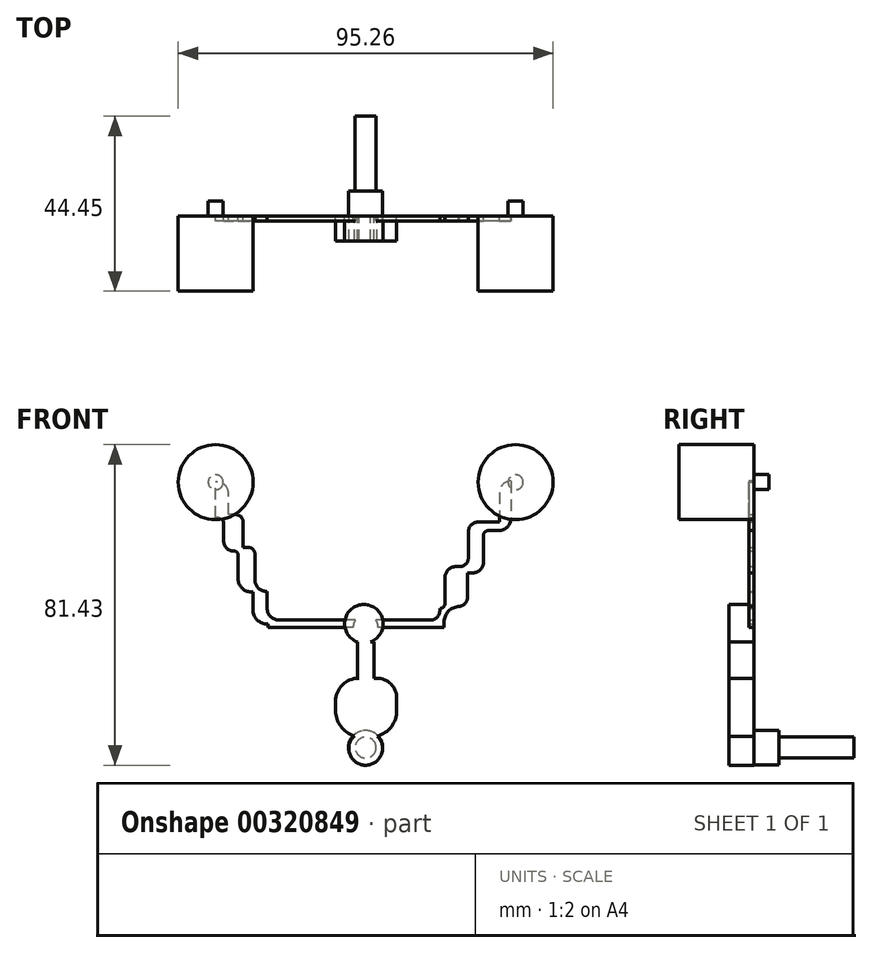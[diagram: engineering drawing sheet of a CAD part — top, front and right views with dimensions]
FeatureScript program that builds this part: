
annotation { "Feature Type Name" : "Feature", "Feature Type Description" : "" }
export const myFeature = defineFeature(function(context is Context, id is Id, definition is map)
    precondition{}
    {
        {
            var Q0;
            Q0=qCreatedBy(makeId("Front.planeOp"),FACE);
            var sketch = newSketch(context, id + "F0", { "sketchPlane" : qUnion([Q0])});
            skCircle(sketch, "E0", {"center": v(-38.1, 36.84) * mm, "radius": 9.53 * mm});
            skCircle(sketch, "E1", {"center": v(38.1, 36.84) * mm, "radius": 9.53 * mm});
            skSolve(sketch);
        }
        {
            var Q0;
            Q0 = qSketchRegion(id + "F0", true);
            var Q1;
            Q1=makeQuery(id+"F0.imprint","IMPRINT",FACE,{"disambiguationData":[TD([[makeQuery(id+"F0.imprint","IMPRINT",EDGE,{"derivedFrom":sQuery(id+"F0.wireOp",EDGE,"W35FGYUQ-ZzTs-Mg4Y-dGm8-Tc2TrGyiYf4W")}),1.0]])]});
            extrude(context, id + "F1", {"entities" : qUnion([Q0, Q1]), "depth" : 19.05 * mm});
        }
        {
            var Q0;
            Q0=qCreatedBy(makeId("Front.planeOp"),FACE);
            var sketch = newSketch(context, id + "F2", { "sketchPlane" : qUnion([Q0])});
            skCircle(sketch, "E2", {"center": v(-38.1, 36.84) * mm, "radius": 1.9 * mm});
            skCircle(sketch, "E3", {"center": v(38.1, 36.84) * mm, "radius": 1.9 * mm});
            skSolve(sketch);
        }
        {
            var Q0;
            Q0 = qSketchRegion(id + "F2", true);
            extrude(context, id + "F3", {"entities" : qUnion([Q0]), "oppositeDirection" : true, "depth" : 3.8 * mm});
        }
        {
            var Q0;
            Q0=qCreatedBy(makeId("Front.planeOp"),FACE);
            var sketch = newSketch(context, id + "F4", { "sketchPlane" : qUnion([Q0])});
            skPoint(sketch, "E4.2.internal.orphan", {"position": v(-38.1, 36.84) * mm});
            skArc(sketch, "E5", {"start": v(3.18, 0) * mm, "mid": v(3.03, 0.94) * mm, "end": v(2.61, 1.8) * mm});
            skLineSegment(sketch, "E6.bottom", {"start": v(36.89, 37.1) * mm, "end": v(36.86, 37.1) * mm});
            skLineSegment(sketch, "E6.top", {"start": v(33.85, 24.55) * mm, "end": v(31.23, 24.55) * mm});
            skLineSegment(sketch, "E6.left", {"start": v(36.86, 37.1) * mm, "end": v(36.86, 27.56) * mm});
            skLineSegment(sketch, "E6.right", {"start": v(34.06, 34.28) * mm, "end": v(34.06, 26.68) * mm});
            skLineSegment(sketch, "E7.bottom", {"start": v(34.06, 26.68) * mm, "end": v(28.54, 26.68) * mm});
            skLineSegment(sketch, "E7.top", {"start": v(27.32, 13.81) * mm, "end": v(25.92, 13.81) * mm});
            skLineSegment(sketch, "E7.left", {"start": v(29.9, 23.2) * mm, "end": v(29.9, 16.39) * mm});
            skLineSegment(sketch, "E7.right", {"start": v(26.1, 24.24) * mm, "end": v(26.1, 17.61) * mm});
            skLineSegment(sketch, "E8.bottom", {"start": v(23.87, 15.39) * mm, "end": v(22.96, 15.39) * mm});
            skLineSegment(sketch, "E8.top", {"start": v(23.82, 5.23) * mm, "end": v(23.53, 5.23) * mm});
            skLineSegment(sketch, "E8.left", {"start": v(25.92, 13.81) * mm, "end": v(25.92, 7.62) * mm});
            skLineSegment(sketch, "E8.right", {"start": v(20.14, 12.56) * mm, "end": v(20.14, 5.93) * mm});
            skLineSegment(sketch, "E9.bottom", {"start": v(19, 4.8) * mm, "end": v(18.83, 4.8) * mm});
            skLineSegment(sketch, "E9.top", {"start": v(19.95, 0) * mm, "end": v(18.83, 0) * mm});
            skLineSegment(sketch, "E9.left", {"start": v(19.95, 1.37) * mm, "end": v(19.95, 0) * mm});
            skLineSegment(sketch, "E9.right", {"start": v(18.83, 4.8) * mm, "end": v(18.83, 4.14) * mm});
            skLineSegment(sketch, "E10.bottom", {"start": v(18.83, 0) * mm, "end": v(2.61, 0) * mm});
            skLineSegment(sketch, "E10.top", {"start": v(16.48, 1.8) * mm, "end": v(2.61, 1.8) * mm});
            skPoint(sketch, "E11.visualSharp", {"position": v(34.06, 37.1) * mm});
            skArc(sketch, "E11.filletArc", {"start": v(36.89, 37.1) * mm, "mid": v(34.89, 36.28) * mm, "end": v(34.06, 34.28) * mm});
            skPoint(sketch, "E12.visualSharp", {"position": v(36.86, 24.55) * mm});
            skArc(sketch, "E12.filletArc", {"start": v(33.85, 24.55) * mm, "mid": v(35.98, 25.43) * mm, "end": v(36.86, 27.56) * mm});
            skPoint(sketch, "E13.visualSharp", {"position": v(29.9, 24.55) * mm});
            skArc(sketch, "E13.filletArc", {"start": v(31.23, 24.55) * mm, "mid": v(30.29, 24.15) * mm, "end": v(29.9, 23.2) * mm});
            skPoint(sketch, "E14.visualSharp", {"position": v(29.9, 13.81) * mm});
            skArc(sketch, "E14.filletArc", {"start": v(27.32, 13.81) * mm, "mid": v(29.14, 14.57) * mm, "end": v(29.9, 16.39) * mm});
            skPoint(sketch, "E15.visualSharp", {"position": v(26.1, 15.39) * mm});
            skArc(sketch, "E15.filletArc", {"start": v(23.87, 15.39) * mm, "mid": v(25.44, 16.04) * mm, "end": v(26.1, 17.61) * mm});
            skPoint(sketch, "E16.visualSharp", {"position": v(26.1, 26.68) * mm});
            skArc(sketch, "E16.filletArc", {"start": v(28.54, 26.68) * mm, "mid": v(26.8, 25.97) * mm, "end": v(26.1, 24.24) * mm});
            skPoint(sketch, "E17.visualSharp", {"position": v(20.14, 15.39) * mm});
            skArc(sketch, "E17.filletArc", {"start": v(22.96, 15.39) * mm, "mid": v(20.97, 14.56) * mm, "end": v(20.14, 12.56) * mm});
            skPoint(sketch, "E18.visualSharp", {"position": v(25.92, 5.23) * mm});
            skArc(sketch, "E18.filletArc", {"start": v(23.53, 5.23) * mm, "mid": v(25.22, 5.93) * mm, "end": v(25.92, 7.62) * mm});
            skPoint(sketch, "E19.visualSharp", {"position": v(19.95, 5.23) * mm});
            skArc(sketch, "E19.filletArc", {"start": v(23.82, 5.23) * mm, "mid": v(21.08, 4.1) * mm, "end": v(19.95, 1.37) * mm});
            skPoint(sketch, "E20.visualSharp", {"position": v(20.14, 4.8) * mm});
            skArc(sketch, "E20.filletArc", {"start": v(19, 4.8) * mm, "mid": v(19.8, 5.13) * mm, "end": v(20.14, 5.93) * mm});
            skPoint(sketch, "E21.visualSharp", {"position": v(18.83, 1.8) * mm});
            skArc(sketch, "E21.filletArc", {"start": v(16.48, 1.8) * mm, "mid": v(18.14, 2.49) * mm, "end": v(18.83, 4.14) * mm});
            skLineSegment(sketch, "E22.bottom", {"start": v(-2.61, 1.8) * mm, "end": v(-22.03, 1.8) * mm});
            skLineSegment(sketch, "E22.top", {"start": v(-2.61, 0) * mm, "end": v(-24.78, 0) * mm});
            skLineSegment(sketch, "E22.right", {"start": v(-24.78, 0.77) * mm, "end": v(-24.78, 0) * mm});
            skLineSegment(sketch, "E23.bottom", {"start": v(-24.78, 0.77) * mm, "end": v(-24.93, 0.77) * mm});
            skLineSegment(sketch, "E23.top", {"start": v(-25.04, 9.09) * mm, "end": v(-25.27, 9.09) * mm});
            skLineSegment(sketch, "E23.left", {"start": v(-25.04, 4.81) * mm, "end": v(-25.04, 9.09) * mm});
            skLineSegment(sketch, "E23.right", {"start": v(-28.63, 4.47) * mm, "end": v(-28.63, 9) * mm});
            skLineSegment(sketch, "E24.bottom", {"start": v(-28.63, 9) * mm, "end": v(-29.16, 9) * mm});
            skLineSegment(sketch, "E24.top", {"start": v(-29.94, 20.3) * mm, "end": v(-31.17, 20.3) * mm});
            skLineSegment(sketch, "E24.left", {"start": v(-28.1, 11.92) * mm, "end": v(-28.1, 18.45) * mm});
            skLineSegment(sketch, "E24.right", {"start": v(-32.4, 12.23) * mm, "end": v(-32.4, 18.33) * mm});
            skLineSegment(sketch, "E25.bottom", {"start": v(-33.4, 19.33) * mm, "end": v(-33.55, 19.33) * mm});
            skLineSegment(sketch, "E25.top", {"start": v(-32.95, 28.61) * mm, "end": v(-34.85, 28.61) * mm});
            skLineSegment(sketch, "E25.left", {"start": v(-31.17, 20.3) * mm, "end": v(-31.17, 26.83) * mm});
            skLineSegment(sketch, "E25.right", {"start": v(-36.07, 21.85) * mm, "end": v(-36.07, 26.34) * mm});
            skLineSegment(sketch, "E26.bottom", {"start": v(-37.56, 27.82) * mm, "end": v(-38.1, 27.82) * mm});
            skLineSegment(sketch, "E26.top", {"start": v(-37.6, 36.84) * mm, "end": v(-38.1, 36.84) * mm});
            skLineSegment(sketch, "E26.left", {"start": v(-34.85, 28.61) * mm, "end": v(-34.85, 34.08) * mm});
            skLineSegment(sketch, "E26.right", {"start": v(-38.1, 27.82) * mm, "end": v(-38.1, 36.84) * mm});
            skPoint(sketch, "E27.visualSharp", {"position": v(-34.85, 36.84) * mm});
            skArc(sketch, "E27.filletArc", {"start": v(-34.85, 34.08) * mm, "mid": v(-35.65, 36.03) * mm, "end": v(-37.6, 36.84) * mm});
            skPoint(sketch, "E28.visualSharp", {"position": v(-36.07, 27.82) * mm});
            skArc(sketch, "E28.filletArc", {"start": v(-36.07, 26.34) * mm, "mid": v(-36.5, 27.39) * mm, "end": v(-37.56, 27.82) * mm});
            skPoint(sketch, "E29.visualSharp", {"position": v(-31.17, 28.61) * mm});
            skArc(sketch, "E29.filletArc", {"start": v(-31.17, 26.83) * mm, "mid": v(-31.7, 28.09) * mm, "end": v(-32.95, 28.61) * mm});
            skPoint(sketch, "E30.visualSharp", {"position": v(-36.07, 19.33) * mm});
            skArc(sketch, "E30.filletArc", {"start": v(-36.07, 21.85) * mm, "mid": v(-35.33, 20.07) * mm, "end": v(-33.55, 19.33) * mm});
            skPoint(sketch, "E31.visualSharp", {"position": v(-28.1, 20.3) * mm});
            skArc(sketch, "E31.filletArc", {"start": v(-28.1, 18.45) * mm, "mid": v(-28.64, 19.75) * mm, "end": v(-29.94, 20.3) * mm});
            skPoint(sketch, "E32.visualSharp", {"position": v(-32.4, 19.33) * mm});
            skArc(sketch, "E32.filletArc", {"start": v(-32.4, 18.33) * mm, "mid": v(-32.7, 19.04) * mm, "end": v(-33.4, 19.33) * mm});
            skPoint(sketch, "E33.visualSharp", {"position": v(-32.4, 9) * mm});
            skArc(sketch, "E33.filletArc", {"start": v(-32.4, 12.23) * mm, "mid": v(-31.45, 9.95) * mm, "end": v(-29.16, 9) * mm});
            skPoint(sketch, "E34.visualSharp", {"position": v(-28.1, 9.09) * mm});
            skArc(sketch, "E34.filletArc", {"start": v(-28.1, 11.92) * mm, "mid": v(-27.27, 9.92) * mm, "end": v(-25.27, 9.09) * mm});
            skPoint(sketch, "E35.visualSharp", {"position": v(-28.63, 0.77) * mm});
            skArc(sketch, "E35.filletArc", {"start": v(-28.63, 4.47) * mm, "mid": v(-27.55, 1.85) * mm, "end": v(-24.93, 0.77) * mm});
            skPoint(sketch, "E36.visualSharp", {"position": v(-25.04, 1.8) * mm});
            skArc(sketch, "E36.filletArc", {"start": v(-25.04, 4.81) * mm, "mid": v(-24.16, 2.68) * mm, "end": v(-22.03, 1.8) * mm});
            skArc(sketch, "E37.trimOffspring", {"start": v(-2.61, 1.8) * mm, "mid": v(-3.03, 0.94) * mm, "end": v(-3.18, 0) * mm});
            skSolve(sketch);
        }
        {
            var Q0;
            Q0 = qSketchRegion(id + "F4", true);
            extrude(context, id + "F5", {"entities" : qUnion([Q0]), "depth" : 1.27 * mm});
        }
        {
            var Q0;
            Q0=qCreatedBy(makeId("Front.planeOp"),FACE);
            var sketch = newSketch(context, id + "F6", { "sketchPlane" : qUnion([Q0])});
            skCircle(sketch, "E38", {"center": v(-0.44, 0.86) * mm, "radius": 4.9 * mm});
            skLineSegment(sketch, "E39.bottom", {"start": v(-2.12, -3.74) * mm, "end": v(2.15, -3.74) * mm});
            skLineSegment(sketch, "E39.top", {"start": v(-2.12, -12.95) * mm, "end": v(2.15, -12.95) * mm});
            skLineSegment(sketch, "E39.left", {"start": v(-2.12, -3.74) * mm, "end": v(-2.12, -12.95) * mm});
            skLineSegment(sketch, "E39.right", {"start": v(2.15, -3.74) * mm, "end": v(2.15, -12.95) * mm});
            skLineSegment(sketch, "E40.bottom", {"start": v(-1.75, -12.95) * mm, "end": v(2.74, -12.95) * mm});
            skLineSegment(sketch, "E40.top", {"start": v(-0.9, -27.92) * mm, "end": v(1.18, -27.92) * mm});
            skLineSegment(sketch, "E40.left", {"start": v(-7.63, -18.84) * mm, "end": v(-7.63, -21.19) * mm});
            skLineSegment(sketch, "E40.right", {"start": v(7.9, -18.12) * mm, "end": v(7.9, -21.19) * mm});
            skPoint(sketch, "E41.visualSharp", {"position": v(7.9, -12.95) * mm});
            skArc(sketch, "E41.filletArc", {"start": v(7.9, -18.12) * mm, "mid": v(6.4, -14.46) * mm, "end": v(2.74, -12.95) * mm});
            skPoint(sketch, "E42.visualSharp", {"position": v(-7.63, -12.95) * mm});
            skArc(sketch, "E42.filletArc", {"start": v(-1.75, -12.95) * mm, "mid": v(-5.9, -14.67) * mm, "end": v(-7.63, -18.84) * mm});
            skPoint(sketch, "E43.visualSharp", {"position": v(7.9, -27.92) * mm});
            skArc(sketch, "E43.filletArc", {"start": v(1.18, -27.92) * mm, "mid": v(5.94, -25.95) * mm, "end": v(7.9, -21.19) * mm});
            skPoint(sketch, "E44.visualSharp", {"position": v(-7.63, -27.92) * mm});
            skArc(sketch, "E44.filletArc", {"start": v(-7.63, -21.19) * mm, "mid": v(-5.66, -25.95) * mm, "end": v(-0.9, -27.92) * mm});
            skSolve(sketch);
        }
        {
            var Q0;
            Q0 = qSketchRegion(id + "F6", true);
            extrude(context, id + "F7", {"entities" : qUnion([Q0]), "depth" : 6.35 * mm});
        }
        {
            var Q0;
            Q0=qCreatedBy(makeId("Front.planeOp"),FACE);
            var sketch = newSketch(context, id + "F8", { "sketchPlane" : qUnion([Q0])});
            skCircle(sketch, "E45", {"center": v(0, -30.58) * mm, "radius": 4.34 * mm});
            skSolve(sketch);
        }
        {
            var Q0;
            Q0 = qSketchRegion(id + "F8", true);
            extrude(context, id + "F9", {"entities" : qUnion([Q0]), "oppositeDirection" : true, "depth" : 6.35 * mm});
        }
        {
            var Q0;
            Q0=qCreatedBy(makeId("Front.planeOp"),FACE);
            var sketch = newSketch(context, id + "F10", { "sketchPlane" : qUnion([Q0])});
            skCircle(sketch, "E46", {"center": v(0, -30.8) * mm, "radius": 4.28 * mm});
            skSolve(sketch);
        }
        {
            var Q0;
            Q0 = qSketchRegion(id + "F10", true);
            extrude(context, id + "F11", {"entities" : qUnion([Q0]), "operationType" : NewBodyOperationType.ADD, "depth" : 6.35 * mm});
        }
        {
            var Q0;
            Q0=qCreatedBy(makeId("Front.planeOp"),FACE);
            var sketch = newSketch(context, id + "F12", { "sketchPlane" : qUnion([Q0])});
            skCircle(sketch, "E47", {"center": v(0, -30.58) * mm, "radius": 2.65 * mm});
            skSolve(sketch);
        }
        {
            var Q0;
            Q0 = qSketchRegion(id + "F12", true);
            extrude(context, id + "F13", {"entities" : qUnion([Q0]), "operationType" : NewBodyOperationType.ADD, "oppositeDirection" : true, "depth" : 25.4 * mm});
        }
    });
